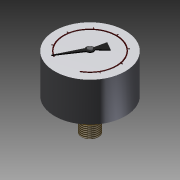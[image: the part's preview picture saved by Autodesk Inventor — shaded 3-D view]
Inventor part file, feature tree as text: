
AUTODESK INVENTOR PART (.ipt)
format: ipt  version: 2014 (Build 180170000, 170)  size: 161,280 bytes
history: native  units: mm
features: imported_body x1, thread x1
ambient origin geometry x8: Origin, YZ Plane, XZ Plane, XY Plane, X Axis, Y Axis, Z Axis, Center Point
bodies: Solid1 (feature_tree)
feature tree (2):
  imported_body  "Base1"
  thread  "Thread1"  [1 undecoded]
note: 1 required parameter value undecoded (feature->parameter linkage not recoverable at this tier; creation-order binding heuristic only, values carry confidence <= 0.55)
